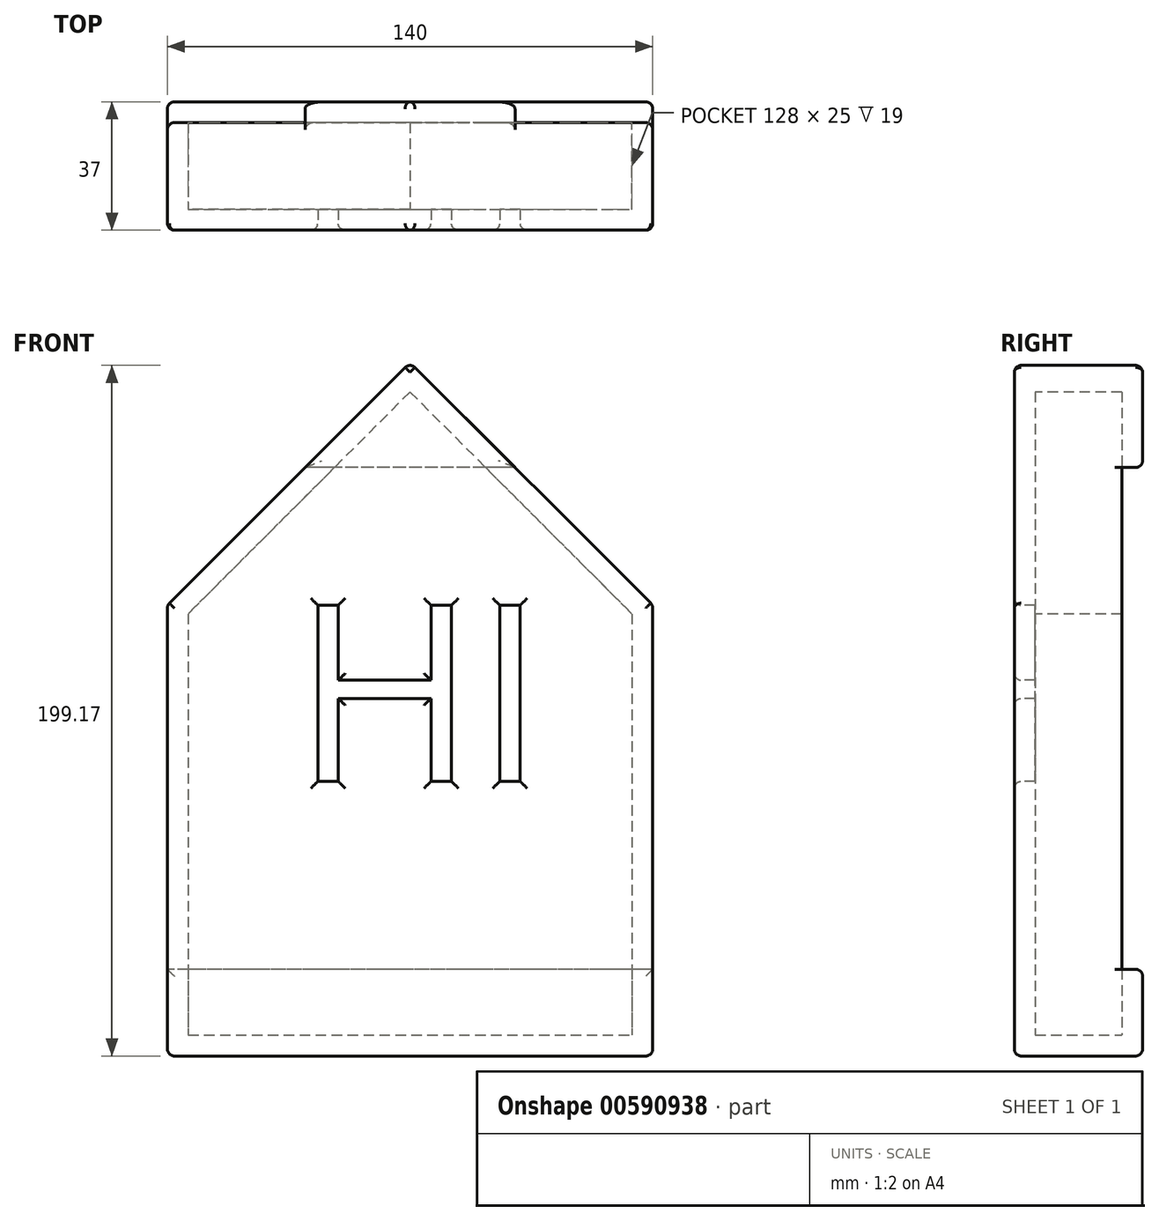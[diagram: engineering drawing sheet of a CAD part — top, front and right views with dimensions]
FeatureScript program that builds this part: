
annotation { "Feature Type Name" : "Feature", "Feature Type Description" : "" }
export const myFeature = defineFeature(function(context is Context, id is Id, definition is map)
    precondition{}
    {
        {
            var Q0;
            Q0=qCreatedBy(makeId("Front.planeOp"),FACE);
            var sketch = newSketch(context, id + "F0", { "sketchPlane" : qUnion([Q0])});
            skLineSegment(sketch, "E0.bottom", {"start": v(-70, 100) * mm, "end": v(70, 100) * mm});
            skLineSegment(sketch, "E0.top", {"start": v(-70, -100) * mm, "end": v(70, -100) * mm});
            skLineSegment(sketch, "E0.left", {"start": v(-70, 100) * mm, "end": v(-70, -100) * mm});
            skLineSegment(sketch, "E0.right", {"start": v(70, 100) * mm, "end": v(70, -100) * mm});
            skPoint(sketch, "E0.middle", {"position": v(0, 0) * mm});
            skSolve(sketch);
        }
        {
            var Q0;
            Q0=makeQuery(id+"F0.imprint","IMPRINT",FACE,{"disambiguationData":[TD([[makeQuery(id+"F0.imprint","IMPRINT",EDGE,{"derivedFrom":sQuery(id+"F0.wireOp",EDGE,"E0.bottom")}),-1.0]])]});
            extrude(context, id + "F1", {"entities" : qUnion([Q0]), "depth" : 6 * mm, "offsetDistance" : 25 * mm});
        }
        {
            var Q0;
            Q0=makeQuery(id+"F1.opExtrude","CAP_FACE",FACE,{"disambiguationData":[OSD([sQuery(id+"F0.wireOp",EDGE,"E0.bottom"),sQuery(id+"F0.wireOp",EDGE,"E0.top"),sQuery(id+"F0.wireOp",EDGE,"E0.left"),sQuery(id+"F0.wireOp",EDGE,"E0.right")])],"isStart":false});
            var sketch = newSketch(context, id + "F2", { "sketchPlane" : qUnion([Q0])});
            skLineSegment(sketch, "E1", {"start": v(0, 100) * mm, "end": v(70, 30) * mm});
            skLineSegment(sketch, "E2", {"start": v(70, 30) * mm, "end": v(70, 100) * mm});
            skLineSegment(sketch, "E3", {"start": v(70, 100) * mm, "end": v(0, 100) * mm});
            skLineSegment(sketch, "E4.MirrorCS", {"start": v(-70, 100) * mm, "end": v(0, 100) * mm});
            skLineSegment(sketch, "E5.MirrorCS", {"start": v(0, 100) * mm, "end": v(-70, 30) * mm});
            skLineSegment(sketch, "E6.MirrorCS", {"start": v(-70, 30) * mm, "end": v(-70, 100) * mm});
            skSolve(sketch);
        }
        {
            var Q0;
            Q0=makeQuery(id+"F2.imprint","IMPRINT",FACE,{"disambiguationData":[TD([[makeQuery(id+"F2.imprint","IMPRINT",EDGE,{"derivedFrom":sQuery(id+"F2.wireOp",EDGE,"E4.MirrorCS")}),-1.0]])]});
            var Q1;
            Q1=makeQuery(id+"F2.imprint","IMPRINT",FACE,{"disambiguationData":[TD([[makeQuery(id+"F2.imprint","IMPRINT",EDGE,{"derivedFrom":sQuery(id+"F2.wireOp",EDGE,"E1")}),1.0]])]});
            extrude(context, id + "F3", {"entities" : qUnion([Q0, Q1]), "operationType" : NewBodyOperationType.REMOVE, "oppositeDirection" : true, "depth" : 25 * mm, "offsetDistance" : 25 * mm});
        }
        {
            var Q0;
            Q0=makeQuery(id+"F1.opExtrude","CAP_FACE",FACE,{"disambiguationData":[OSD([sQuery(id+"F0.wireOp",EDGE,"E0.bottom"),sQuery(id+"F0.wireOp",EDGE,"E0.top"),sQuery(id+"F0.wireOp",EDGE,"E0.left"),sQuery(id+"F0.wireOp",EDGE,"E0.right")])],"isStart":false});
            var sketch = newSketch(context, id + "F4", { "sketchPlane" : qUnion([Q0])});
            skText(sketch, "E7", { "text": "HI", "fontName": "OpenSans-Regular.ttf"});
            const initialGuessF4  = {"E7": [-0.0336, -0.0208, 1, 0, 0.05123]};
            skSetInitialGuess(sketch, initialGuessF4);
            skSolve(sketch);
        }
        {
            var Q0;
            Q0 = qSketchRegion(id + "F4", true);
            extrude(context, id + "F5", {"entities" : qUnion([Q0]), "operationType" : NewBodyOperationType.REMOVE, "oppositeDirection" : true, "depth" : 25 * mm, "offsetDistance" : 25 * mm});
        }
        {
            var Q0;
            Q0=makeQuery(id+"F1.opExtrude","CAP_FACE",FACE,{"disambiguationData":[OSD([sQuery(id+"F0.wireOp",EDGE,"E0.bottom"),sQuery(id+"F0.wireOp",EDGE,"E0.top"),sQuery(id+"F0.wireOp",EDGE,"E0.left"),sQuery(id+"F0.wireOp",EDGE,"E0.right")])],"isStart":true});
            var sketch = newSketch(context, id + "F6", { "sketchPlane" : qUnion([Q0])});
            skLineSegment(sketch, "E8", {"start": v(-70, -100) * mm, "end": v(-70, 30) * mm});
            skLineSegment(sketch, "E9", {"start": v(-70, 30) * mm, "end": v(0, 100) * mm});
            skLineSegment(sketch, "E10", {"start": v(0, 100) * mm, "end": v(70, 30) * mm});
            skLineSegment(sketch, "E11", {"start": v(70, 30) * mm, "end": v(70, -100) * mm});
            skLineSegment(sketch, "E12", {"start": v(70, -100) * mm, "end": v(-70, -100) * mm});
            skSolve(sketch);
        }
        {
            var Q0;
            Q0=makeQuery(id+"F6.imprint","IMPRINT",FACE,{"disambiguationData":[TD([[makeQuery(id+"F6.imprint","IMPRINT",EDGE,{"derivedFrom":sQuery(id+"F6.wireOp",EDGE,"E8")}),1.0]])]});
            extrude(context, id + "F7", {"entities" : qUnion([Q0]), "operationType" : NewBodyOperationType.ADD, "depth" : 25 * mm, "offsetDistance" : 25 * mm});
        }
        {
            var Q0;
            Q0=makeQuery(id+"F7.opExtrude","CAP_FACE",FACE,{"disambiguationData":[OSD([sQuery(id+"F0.wireOp",EDGE,"E0.bottom"),sQuery(id+"F0.wireOp",EDGE,"E0.top"),sQuery(id+"F0.wireOp",EDGE,"E0.left"),sQuery(id+"F0.wireOp",EDGE,"E0.right"),sQuery(id+"F4.wireOp",EDGE,"E7.sketch_text.stroke-0"),sQuery(id+"F4.wireOp",EDGE,"E7.sketch_text.stroke-1"),sQuery(id+"F4.wireOp",EDGE,"E7.sketch_text.stroke-2"),sQuery(id+"F4.wireOp",EDGE,"E7.sketch_text.stroke-3"),sQuery(id+"F4.wireOp",EDGE,"E7.sketch_text.stroke-4"),sQuery(id+"F4.wireOp",EDGE,"E7.sketch_text.stroke-5"),sQuery(id+"F4.wireOp",EDGE,"E7.sketch_text.stroke-6"),sQuery(id+"F4.wireOp",EDGE,"E7.sketch_text.stroke-7"),sQuery(id+"F4.wireOp",EDGE,"E7.sketch_text.stroke-8"),sQuery(id+"F4.wireOp",EDGE,"E7.sketch_text.stroke-9"),sQuery(id+"F4.wireOp",EDGE,"E7.sketch_text.stroke-10"),sQuery(id+"F4.wireOp",EDGE,"E7.sketch_text.stroke-11"),sQuery(id+"F4.wireOp",EDGE,"E7.sketch_text.stroke-12"),sQuery(id+"F4.wireOp",EDGE,"E7.sketch_text.stroke-13"),sQuery(id+"F4.wireOp",EDGE,"E7.sketch_text.stroke-14"),sQuery(id+"F4.wireOp",EDGE,"E7.sketch_text.stroke-15"),sQuery(id+"F6.wireOp",EDGE,"E8"),sQuery(id+"F6.wireOp",EDGE,"E9"),sQuery(id+"F6.wireOp",EDGE,"E10"),sQuery(id+"F6.wireOp",EDGE,"E11"),sQuery(id+"F6.wireOp",EDGE,"E12")])],"isStart":false});
            shell(context, id + "F8", {"entities" : qUnion([Q0]), "thickness" : 6 * mm});
        }
        {
            var Q0;
            Q0=makeQuery(id+"F8.opShell","OFFSET_FACE",FACE,{"disambiguationData":[OSD([sQuery(id+"F0.wireOp",EDGE,"E0.bottom"),sQuery(id+"F0.wireOp",EDGE,"E0.top"),sQuery(id+"F0.wireOp",EDGE,"E0.left"),sQuery(id+"F0.wireOp",EDGE,"E0.right"),sQuery(id+"F4.wireOp",EDGE,"E7.sketch_text.stroke-0"),sQuery(id+"F4.wireOp",EDGE,"E7.sketch_text.stroke-1"),sQuery(id+"F4.wireOp",EDGE,"E7.sketch_text.stroke-2"),sQuery(id+"F4.wireOp",EDGE,"E7.sketch_text.stroke-3"),sQuery(id+"F4.wireOp",EDGE,"E7.sketch_text.stroke-4"),sQuery(id+"F4.wireOp",EDGE,"E7.sketch_text.stroke-5"),sQuery(id+"F4.wireOp",EDGE,"E7.sketch_text.stroke-6"),sQuery(id+"F4.wireOp",EDGE,"E7.sketch_text.stroke-7"),sQuery(id+"F4.wireOp",EDGE,"E7.sketch_text.stroke-8"),sQuery(id+"F4.wireOp",EDGE,"E7.sketch_text.stroke-9"),sQuery(id+"F4.wireOp",EDGE,"E7.sketch_text.stroke-10"),sQuery(id+"F4.wireOp",EDGE,"E7.sketch_text.stroke-11"),sQuery(id+"F4.wireOp",EDGE,"E7.sketch_text.stroke-12"),sQuery(id+"F4.wireOp",EDGE,"E7.sketch_text.stroke-13"),sQuery(id+"F4.wireOp",EDGE,"E7.sketch_text.stroke-14"),sQuery(id+"F4.wireOp",EDGE,"E7.sketch_text.stroke-15"),sQuery(id+"F6.wireOp",EDGE,"E8"),sQuery(id+"F6.wireOp",EDGE,"E9"),sQuery(id+"F6.wireOp",EDGE,"E10"),sQuery(id+"F6.wireOp",EDGE,"E11"),sQuery(id+"F6.wireOp",EDGE,"E12")]),OD(1.0)]});
            var sketch = newSketch(context, id + "F9", { "sketchPlane" : qUnion([Q0])});
            skLineSegment(sketch, "E13", {"start": v(-39.19, 38.13) * mm, "end": v(37, 38.13) * mm});
            skLineSegment(sketch, "E14", {"start": v(37, 38.13) * mm, "end": v(37, -31.84) * mm});
            skLineSegment(sketch, "E15", {"start": v(37, -31.84) * mm, "end": v(-40.65, -31.84) * mm});
            skLineSegment(sketch, "E16", {"start": v(-40.65, -31.84) * mm, "end": v(-39.19, 38.13) * mm});
            skSolve(sketch);
        }
        {
            var Q0;
            Q0=makeQuery(id+"F9.imprint","IMPRINT",FACE,{"disambiguationData":[TD([[makeQuery(id+"F9.imprint","IMPRINT",EDGE,{"derivedFrom":sQuery(id+"F9.wireOp",EDGE,"E13")}),-1.0]])]});
            extrude(context, id + "F10", {"entities" : qUnion([Q0]), "operationType" : NewBodyOperationType.REMOVE, "oppositeDirection" : true, "depth" : 25 * mm, "offsetDistance" : 25 * mm});
        }
        {
            var Q0;
            Q0=makeQuery(id+"F8.opShell","OFFSET_FACE",FACE,{"disambiguationData":[OSD([sQuery(id+"F0.wireOp",EDGE,"E0.bottom"),sQuery(id+"F0.wireOp",EDGE,"E0.top"),sQuery(id+"F0.wireOp",EDGE,"E0.left"),sQuery(id+"F0.wireOp",EDGE,"E0.right"),sQuery(id+"F4.wireOp",EDGE,"E7.sketch_text.stroke-0"),sQuery(id+"F4.wireOp",EDGE,"E7.sketch_text.stroke-1"),sQuery(id+"F4.wireOp",EDGE,"E7.sketch_text.stroke-2"),sQuery(id+"F4.wireOp",EDGE,"E7.sketch_text.stroke-3"),sQuery(id+"F4.wireOp",EDGE,"E7.sketch_text.stroke-4"),sQuery(id+"F4.wireOp",EDGE,"E7.sketch_text.stroke-5"),sQuery(id+"F4.wireOp",EDGE,"E7.sketch_text.stroke-6"),sQuery(id+"F4.wireOp",EDGE,"E7.sketch_text.stroke-7"),sQuery(id+"F4.wireOp",EDGE,"E7.sketch_text.stroke-8"),sQuery(id+"F4.wireOp",EDGE,"E7.sketch_text.stroke-9"),sQuery(id+"F4.wireOp",EDGE,"E7.sketch_text.stroke-10"),sQuery(id+"F4.wireOp",EDGE,"E7.sketch_text.stroke-11"),sQuery(id+"F4.wireOp",EDGE,"E7.sketch_text.stroke-12"),sQuery(id+"F4.wireOp",EDGE,"E7.sketch_text.stroke-13"),sQuery(id+"F4.wireOp",EDGE,"E7.sketch_text.stroke-14"),sQuery(id+"F4.wireOp",EDGE,"E7.sketch_text.stroke-15"),sQuery(id+"F6.wireOp",EDGE,"E8"),sQuery(id+"F6.wireOp",EDGE,"E9"),sQuery(id+"F6.wireOp",EDGE,"E10"),sQuery(id+"F6.wireOp",EDGE,"E11"),sQuery(id+"F6.wireOp",EDGE,"E12")]),OD(1.0)]});
            extrude(context, id + "F11", {"entities" : qUnion([Q0]), "operationType" : NewBodyOperationType.REMOVE, "oppositeDirection" : true, "depth" : 25 * mm, "offsetDistance" : 25 * mm});
        }
        {
            var Q0;
            Q0=makeQuery(id+"F8.opShell","OFFSET_FACE",FACE,{"disambiguationData":[OSD([sQuery(id+"F0.wireOp",EDGE,"E0.bottom"),sQuery(id+"F0.wireOp",EDGE,"E0.top"),sQuery(id+"F0.wireOp",EDGE,"E0.left"),sQuery(id+"F0.wireOp",EDGE,"E0.right"),sQuery(id+"F4.wireOp",EDGE,"E7.sketch_text.stroke-0"),sQuery(id+"F4.wireOp",EDGE,"E7.sketch_text.stroke-1"),sQuery(id+"F4.wireOp",EDGE,"E7.sketch_text.stroke-2"),sQuery(id+"F4.wireOp",EDGE,"E7.sketch_text.stroke-3"),sQuery(id+"F4.wireOp",EDGE,"E7.sketch_text.stroke-4"),sQuery(id+"F4.wireOp",EDGE,"E7.sketch_text.stroke-5"),sQuery(id+"F4.wireOp",EDGE,"E7.sketch_text.stroke-6"),sQuery(id+"F4.wireOp",EDGE,"E7.sketch_text.stroke-7"),sQuery(id+"F4.wireOp",EDGE,"E7.sketch_text.stroke-8"),sQuery(id+"F4.wireOp",EDGE,"E7.sketch_text.stroke-9"),sQuery(id+"F4.wireOp",EDGE,"E7.sketch_text.stroke-10"),sQuery(id+"F4.wireOp",EDGE,"E7.sketch_text.stroke-11"),sQuery(id+"F4.wireOp",EDGE,"E7.sketch_text.stroke-12"),sQuery(id+"F4.wireOp",EDGE,"E7.sketch_text.stroke-13"),sQuery(id+"F4.wireOp",EDGE,"E7.sketch_text.stroke-14"),sQuery(id+"F4.wireOp",EDGE,"E7.sketch_text.stroke-15"),sQuery(id+"F6.wireOp",EDGE,"E8"),sQuery(id+"F6.wireOp",EDGE,"E9"),sQuery(id+"F6.wireOp",EDGE,"E10"),sQuery(id+"F6.wireOp",EDGE,"E11"),sQuery(id+"F6.wireOp",EDGE,"E12")]),OD(0.0)]});
            var sketch = newSketch(context, id + "F12", { "sketchPlane" : qUnion([Q0])});
            skLineSegment(sketch, "E17.bottom", {"start": v(-70, -100) * mm, "end": v(70, -100) * mm});
            skLineSegment(sketch, "E17.top", {"start": v(-70, -75) * mm, "end": v(70, -75) * mm});
            skLineSegment(sketch, "E17.left", {"start": v(-70, -100) * mm, "end": v(-70, -75) * mm});
            skLineSegment(sketch, "E17.right", {"start": v(70, -100) * mm, "end": v(70, -75) * mm});
            skSolve(sketch);
        }
        {
            var Q0;
            Q0 = qSketchRegion(id + "F12", true);
            extrude(context, id + "F13", {"entities" : qUnion([Q0]), "operationType" : NewBodyOperationType.ADD, "depth" : 6 * mm, "offsetDistance" : 25 * mm});
        }
        {
            var Q0;
            Q0=makeQuery(id+"F8.opShell","OFFSET_FACE",FACE,{"disambiguationData":[OSD([sQuery(id+"F0.wireOp",EDGE,"E0.bottom"),sQuery(id+"F0.wireOp",EDGE,"E0.top"),sQuery(id+"F0.wireOp",EDGE,"E0.left"),sQuery(id+"F0.wireOp",EDGE,"E0.right"),sQuery(id+"F4.wireOp",EDGE,"E7.sketch_text.stroke-0"),sQuery(id+"F4.wireOp",EDGE,"E7.sketch_text.stroke-1"),sQuery(id+"F4.wireOp",EDGE,"E7.sketch_text.stroke-2"),sQuery(id+"F4.wireOp",EDGE,"E7.sketch_text.stroke-3"),sQuery(id+"F4.wireOp",EDGE,"E7.sketch_text.stroke-4"),sQuery(id+"F4.wireOp",EDGE,"E7.sketch_text.stroke-5"),sQuery(id+"F4.wireOp",EDGE,"E7.sketch_text.stroke-6"),sQuery(id+"F4.wireOp",EDGE,"E7.sketch_text.stroke-7"),sQuery(id+"F4.wireOp",EDGE,"E7.sketch_text.stroke-8"),sQuery(id+"F4.wireOp",EDGE,"E7.sketch_text.stroke-9"),sQuery(id+"F4.wireOp",EDGE,"E7.sketch_text.stroke-10"),sQuery(id+"F4.wireOp",EDGE,"E7.sketch_text.stroke-11"),sQuery(id+"F4.wireOp",EDGE,"E7.sketch_text.stroke-12"),sQuery(id+"F4.wireOp",EDGE,"E7.sketch_text.stroke-13"),sQuery(id+"F4.wireOp",EDGE,"E7.sketch_text.stroke-14"),sQuery(id+"F4.wireOp",EDGE,"E7.sketch_text.stroke-15"),sQuery(id+"F6.wireOp",EDGE,"E8"),sQuery(id+"F6.wireOp",EDGE,"E9"),sQuery(id+"F6.wireOp",EDGE,"E10"),sQuery(id+"F6.wireOp",EDGE,"E11"),sQuery(id+"F6.wireOp",EDGE,"E12")]),OD(0.0)]});
            var sketch = newSketch(context, id + "F14", { "sketchPlane" : qUnion([Q0])});
            skLineSegment(sketch, "E18", {"start": v(0, 100) * mm, "end": v(-30.29, 69.71) * mm});
            skLineSegment(sketch, "E19", {"start": v(-30.29, 69.71) * mm, "end": v(30.29, 69.71) * mm});
            skLineSegment(sketch, "E20", {"start": v(30.29, 69.71) * mm, "end": v(0, 100) * mm});
            skSolve(sketch);
        }
        {
            var Q0;
            Q0 = qSketchRegion(id + "F14", true);
            extrude(context, id + "F15", {"entities" : qUnion([Q0]), "operationType" : NewBodyOperationType.ADD, "depth" : 6 * mm, "offsetDistance" : 25 * mm});
        }
        {
            var Q0;
            Q0=makeQuery(id+"F1.opExtrude","CAP_FACE",FACE,{"disambiguationData":[OSD([sQuery(id+"F0.wireOp",EDGE,"E0.bottom"),sQuery(id+"F0.wireOp",EDGE,"E0.top"),sQuery(id+"F0.wireOp",EDGE,"E0.left"),sQuery(id+"F0.wireOp",EDGE,"E0.right")])],"isStart":false});
            var Q1;
            Q1=makeQuery(id+"F15.opExtrude","CAP_FACE",FACE,{"disambiguationData":[OSD([sQuery(id+"F14.wireOp",EDGE,"E18"),sQuery(id+"F14.wireOp",EDGE,"E19"),sQuery(id+"F14.wireOp",EDGE,"E20")])],"isStart":false});
            var Q2;
            Q2=makeQuery(id+"F13.opExtrude","CAP_FACE",FACE,{"disambiguationData":[OSD([sQuery(id+"F12.wireOp",EDGE,"E17.bottom"),sQuery(id+"F12.wireOp",EDGE,"E17.top"),sQuery(id+"F12.wireOp",EDGE,"E17.left"),sQuery(id+"F12.wireOp",EDGE,"E17.right")])],"isStart":false});
            fillet(context, id + "F16", {"entities" : qUnion([Q0, Q1, Q2]), "radius" : 2 * mm, "tangentPropagation" : true, "allowEdgeOverflow" : false});
        }
        {
            var Q0;
            Q0=makeQuery(id+"F13.boolean.opBoolean","MERGE",EDGE,{"derivedFrom":[makeQuery(id+"F7.boolean.opBoolean","MERGE",EDGE,{"derivedFrom":[makeQuery(id+"F1.opExtrude","SWEPT_EDGE",EDGE,{"disambiguationData":[OSD([sQuery(id+"F0.wireOp",EDGE,"E0.top"),sQuery(id+"F0.wireOp",EDGE,"E0.right")])]}),makeQuery(id+"F7.opExtrude","SWEPT_EDGE",EDGE,{"disambiguationData":[OSD([sQuery(id+"F6.wireOp",EDGE,"E8"),sQuery(id+"F6.wireOp",EDGE,"E12")])]})]}),makeQuery(id+"F13.opExtrude","SWEPT_EDGE",EDGE,{"disambiguationData":[OSD([sQuery(id+"F12.wireOp",EDGE,"E17.bottom"),sQuery(id+"F12.wireOp",EDGE,"E17.left")])]})]});
            var Q1;
            Q1=makeQuery(id+"F7.opExtrude","CAP_EDGE",EDGE,{"disambiguationData":[OSD([sQuery(id+"F6.wireOp",EDGE,"E8")])],"isStart":false});
            var Q2;
            Q2=makeQuery(id+"F7.boolean.opBoolean","MERGE",EDGE,{"derivedFrom":[makeQuery(id+"F3.boolean.opBoolean","COPY",EDGE,{"derivedFrom":makeQuery(id+"F3.opExtrude","SWEPT_EDGE",EDGE,{"disambiguationData":[OSD([sQuery(id+"F0.wireOp",EDGE,"E0.right"),sQuery(id+"F2.wireOp",EDGE,"E1"),sQuery(id+"F2.wireOp",EDGE,"E2")])]})}),makeQuery(id+"F7.opExtrude","SWEPT_EDGE",EDGE,{"disambiguationData":[OSD([sQuery(id+"F6.wireOp",EDGE,"E8"),sQuery(id+"F6.wireOp",EDGE,"E9")])]})]});
            var Q3;
            {var subQ0=sQuery(id+"F2.wireOp",EDGE,"E5.MirrorCS");var subQ1=sQuery(id+"F2.wireOp",EDGE,"E4.MirrorCS");var subQ2=sQuery(id+"F2.wireOp",EDGE,"E3");var subQ3=sQuery(id+"F2.wireOp",EDGE,"E1");Q3=makeQuery(id+"F15.boolean.opBoolean","MERGE",EDGE,{"derivedFrom":[makeQuery(id+"F7.boolean.opBoolean","MERGE",EDGE,{"derivedFrom":[makeQuery(id+"F3.boolean.opBoolean","TWEAK_EDGE",EDGE,{"derivedFrom":[makeQuery(id+"F3.opExtrude","SWEPT_EDGE",EDGE,{"disambiguationData":[OSD([subQ3,subQ2,subQ1,subQ0]),OD(0.0)]}),makeQuery(id+"F3.opExtrude","SWEPT_EDGE",EDGE,{"disambiguationData":[OSD([subQ3,subQ2,subQ1,subQ0]),OD(1.0)]})]}),makeQuery(id+"F7.opExtrude","SWEPT_EDGE",EDGE,{"disambiguationData":[OSD([sQuery(id+"F6.wireOp",EDGE,"E9"),sQuery(id+"F6.wireOp",EDGE,"E10")])]})]}),makeQuery(id+"F15.opExtrude","SWEPT_EDGE",EDGE,{"disambiguationData":[OSD([sQuery(id+"F14.wireOp",EDGE,"E18"),sQuery(id+"F14.wireOp",EDGE,"E20")])]})]});}
            var Q4;
            Q4=makeQuery(id+"F7.opExtrude","CAP_EDGE",EDGE,{"disambiguationData":[OSD([sQuery(id+"F6.wireOp",EDGE,"E9")])],"isStart":false});
            var Q5;
            Q5=makeQuery(id+"F7.opExtrude","CAP_EDGE",EDGE,{"disambiguationData":[OSD([sQuery(id+"F6.wireOp",EDGE,"E10")])],"isStart":false});
            var Q6;
            Q6=makeQuery(id+"F7.boolean.opBoolean","MERGE",EDGE,{"derivedFrom":[makeQuery(id+"F3.boolean.opBoolean","COPY",EDGE,{"derivedFrom":makeQuery(id+"F3.opExtrude","SWEPT_EDGE",EDGE,{"disambiguationData":[OSD([sQuery(id+"F0.wireOp",EDGE,"E0.left"),sQuery(id+"F2.wireOp",EDGE,"E5.MirrorCS"),sQuery(id+"F2.wireOp",EDGE,"E6.MirrorCS")])]})}),makeQuery(id+"F7.opExtrude","SWEPT_EDGE",EDGE,{"disambiguationData":[OSD([sQuery(id+"F6.wireOp",EDGE,"E10"),sQuery(id+"F6.wireOp",EDGE,"E11")])]})]});
            var Q7;
            {var subQ0=sQuery(id+"F0.wireOp",EDGE,"E0.top");Q7=makeQuery(id+"F16.opFillet","BLEND_EDGE",EDGE,{"blendedFrom":[makeQuery(id+"F1.opExtrude","CAP_EDGE",EDGE,{"disambiguationData":[OSD([subQ0])],"isStart":false}),makeQuery(id+"F13.boolean.opBoolean","MERGE",FACE,{"derivedFrom":[makeQuery(id+"F7.boolean.opBoolean","MERGE",FACE,{"derivedFrom":[makeQuery(id+"F1.opExtrude","SWEPT_FACE",FACE,{"disambiguationData":[OSD([subQ0])]}),makeQuery(id+"F7.opExtrude","SWEPT_FACE",FACE,{"disambiguationData":[OSD([sQuery(id+"F6.wireOp",EDGE,"E12")])]})]}),makeQuery(id+"F13.opExtrude","SWEPT_FACE",FACE,{"disambiguationData":[OSD([sQuery(id+"F12.wireOp",EDGE,"E17.bottom")])]})]})],"blendedInto":[makeQuery(id+"F13.boolean.opBoolean","MERGE",FACE,{"derivedFrom":[makeQuery(id+"F7.boolean.opBoolean","MERGE",FACE,{"derivedFrom":[makeQuery(id+"F1.opExtrude","SWEPT_FACE",FACE,{"disambiguationData":[OSD([subQ0])]}),makeQuery(id+"F7.opExtrude","SWEPT_FACE",FACE,{"disambiguationData":[OSD([sQuery(id+"F6.wireOp",EDGE,"E12")])]})]}),makeQuery(id+"F13.opExtrude","SWEPT_FACE",FACE,{"disambiguationData":[OSD([sQuery(id+"F12.wireOp",EDGE,"E17.bottom")])]})]})]});}
            var Q8;
            Q8=makeQuery(id+"F13.boolean.opBoolean","MERGE",EDGE,{"derivedFrom":[makeQuery(id+"F7.boolean.opBoolean","MERGE",EDGE,{"derivedFrom":[makeQuery(id+"F1.opExtrude","SWEPT_EDGE",EDGE,{"disambiguationData":[OSD([sQuery(id+"F0.wireOp",EDGE,"E0.top"),sQuery(id+"F0.wireOp",EDGE,"E0.left")])]}),makeQuery(id+"F7.opExtrude","SWEPT_EDGE",EDGE,{"disambiguationData":[OSD([sQuery(id+"F6.wireOp",EDGE,"E11"),sQuery(id+"F6.wireOp",EDGE,"E12")])]})]}),makeQuery(id+"F13.opExtrude","SWEPT_EDGE",EDGE,{"disambiguationData":[OSD([sQuery(id+"F12.wireOp",EDGE,"E17.bottom"),sQuery(id+"F12.wireOp",EDGE,"E17.right")])]})]});
            var Q9;
            Q9=makeQuery(id+"F7.opExtrude","CAP_EDGE",EDGE,{"disambiguationData":[OSD([sQuery(id+"F6.wireOp",EDGE,"E11")])],"isStart":false});
            fillet(context, id + "F17", {"entities" : qUnion([Q0, Q1, Q2, Q3, Q4, Q5, Q6, Q7, Q8, Q9]), "radius" : 2 * mm, "tangentPropagation" : true, "allowEdgeOverflow" : false});
        }
    });
